# Revit family: NAU_Naughtone_Stng_Polly_Wood-Stools
name_source: partatom
category: Furniture
revit_build: Autodesk Revit 2015 (Build: 20140903_1530(x64)
units: mm (PartAtom-declared; Revit-internal decimal feet)

## types (2) — shared parameters
Assembly Code = E2020200
AssetType = Moveable
BIMObjectName = NAU_Naughtone_Seating_Polly_Wood-Stools
Category = Pr_40_50_12_85 Stools
Color = Various
DurationUnit = year
Finish = Nonupholstered
IfcExportAs = IfcFurnishingElementType
IfcExportType = STOOL
Keynote = Pr_40_50_12_85
MainColor = Various
ManufacturerAddressUK = Knaresborough Tech Park, Manse Lane, Knaresborough, HG5 8LF
ManufacturerName = Naughtone
ManufacturerURL = www.naughtone.com
Material = Wood/plastic
NBSDescription = Seating
NBSReference = 45-35-72/352
Name = Seating_Polly_Wood-Stools_Naughtone
ProductInformation = www.naughtone.com/portfolio-view/polly
ReplacementCost = 0.00
Shape = Rectangular
SustainabilityPerformance = FISP certified. ISO 14001. SCS indoor advantage gold
URL = www.naughtone.com
Uniclass2015Description = Stools
Uniclass2015Reference = Pr_40_50_12_85
Uniclass2015Version = Products v1.8
Version = 1
WarrantyDurationLabor = 5
WarrantyDurationParts = 5
WarrantyDurationUnit = year

## per-type parameters (varying)
| type | Description | IsPOLLYBSWD | IsPOLLYCHSWD | ModelReference | NominalHeight | NominalLength | NominalWidth | Size |
| POLLYBSWD | Polly Wood Barstool | Yes | No | Polly Wood Barstool | 1070 mm  [stored 3.5105 ft] | 575 mm | 565 mm  [stored 1.85367 ft] | 575 x 565 x 1070mm |
| POLLYCHSWD | Polly Wood Counterheight Stool | No | Yes | Polly Wood Counterheight Stool | 1000 mm  [stored 3.28084 ft] | 560 mm  [stored 1.83727 ft] | 510 mm  [stored 1.67323 ft] | 560 x 510 x 1000mm |

note: column(s) folded — value = type name in every type: Model, ModelNumber

note: [stored X ft] marks values corroborated as IEEE doubles in the binary element streams (Revit-internal decimal feet)

## geometry (parser evidence)
native form markers: Sweep x2
no freeform markers — native parametric forms only
